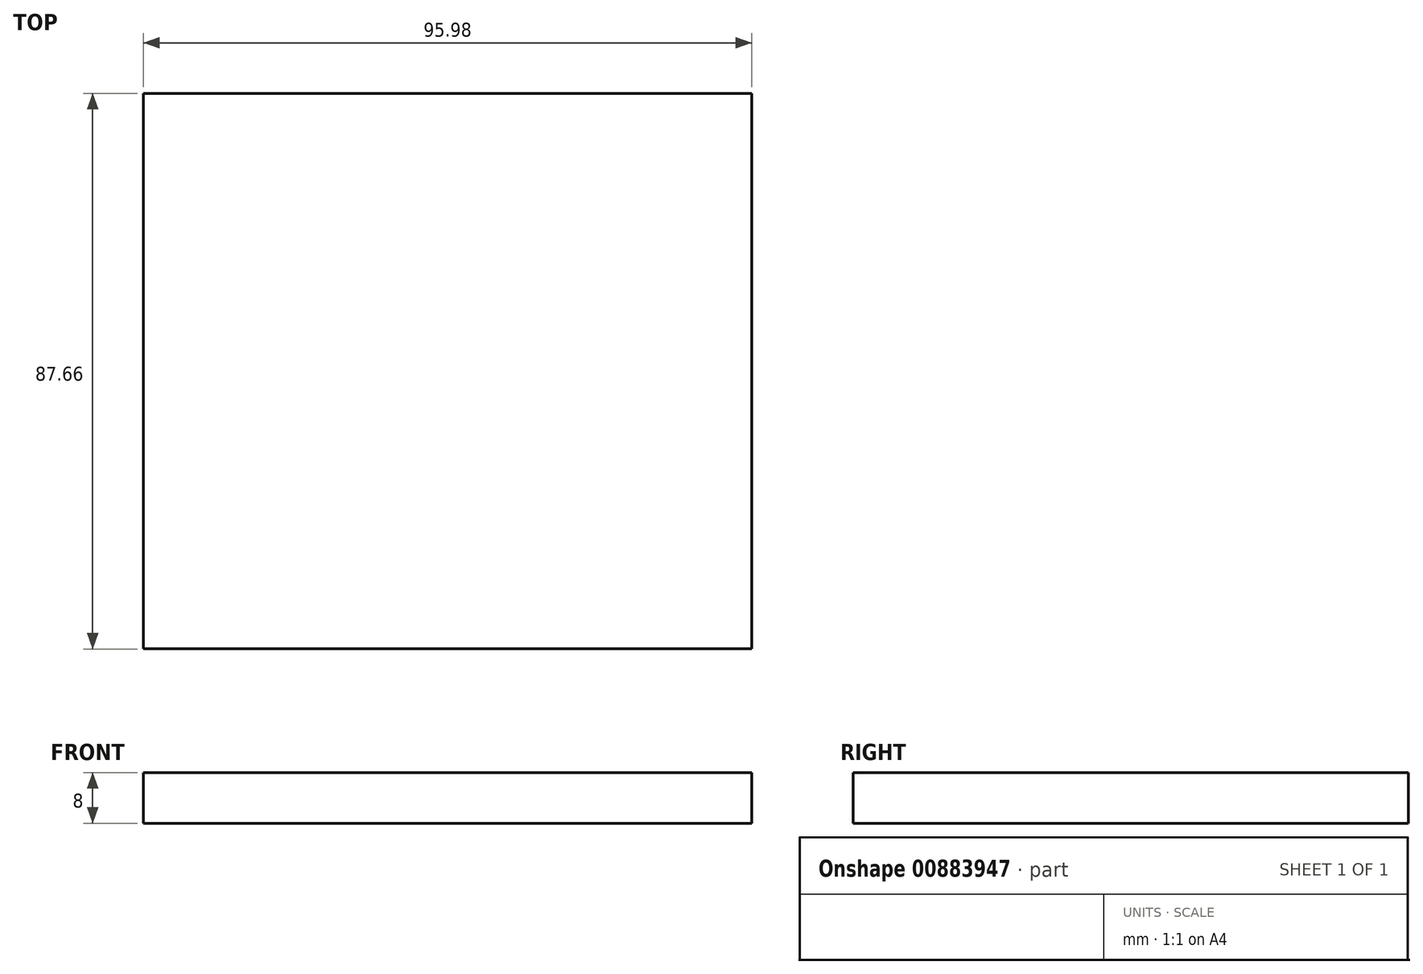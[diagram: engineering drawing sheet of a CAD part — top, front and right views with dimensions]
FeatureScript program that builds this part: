
annotation { "Feature Type Name" : "Feature", "Feature Type Description" : "" }
export const myFeature = defineFeature(function(context is Context, id is Id, definition is map)
    precondition{}
    {
        {
            var Q0;
            Q0=qCreatedBy(makeId("Top.planeOp"),FACE);
            var sketch = newSketch(context, id + "F0", { "sketchPlane" : qUnion([Q0])});
            skLineSegment(sketch, "E0.bottom", {"start": v(48, 43.83) * mm, "end": v(-48, 43.83) * mm});
            skLineSegment(sketch, "E0.top", {"start": v(48, -43.83) * mm, "end": v(-48, -43.83) * mm});
            skLineSegment(sketch, "E0.left", {"start": v(48, 43.83) * mm, "end": v(48, -43.83) * mm});
            skLineSegment(sketch, "E0.right", {"start": v(-48, 43.83) * mm, "end": v(-48, -43.83) * mm});
            skPoint(sketch, "E0.middle", {"position": v(0, 0) * mm});
            skSolve(sketch);
        }
        {
            var Q0;
            Q0 = qSketchRegion(id + "F0", true);
            extrude(context, id + "F1", {"entities" : qUnion([Q0]), "depth" : 8 * mm, "offsetDistance" : 25.4 * mm});
        }
    });
